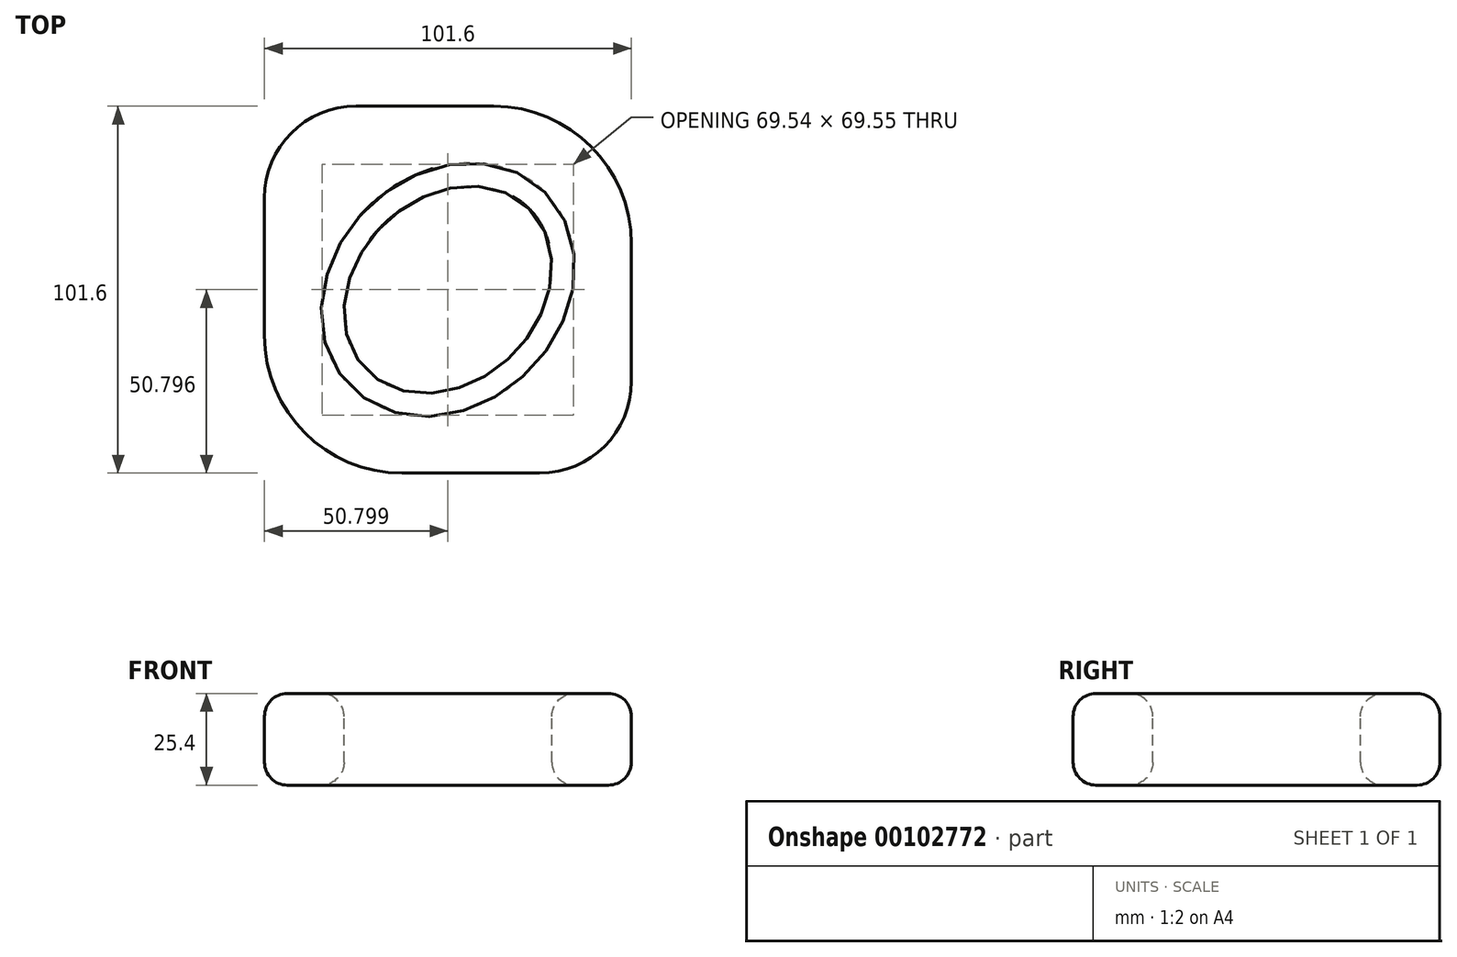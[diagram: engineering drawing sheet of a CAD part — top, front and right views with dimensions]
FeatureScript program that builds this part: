
annotation { "Feature Type Name" : "Feature", "Feature Type Description" : "" }
export const myFeature = defineFeature(function(context is Context, id is Id, definition is map)
    precondition{}
    {
        {
            var Q0;
            Q0=qCreatedBy(makeId("Top.planeOp"),FACE);
            var sketch = newSketch(context, id + "F0", { "sketchPlane" : qUnion([Q0])});
            skEllipse(sketch, "E0", {"center": v(0, 0) * mm, "majorRadius": 31.75 * mm, "minorRadius": 25.4 * mm, "majorAxis": v(0.7, 0.7)});
            skLineSegment(sketch, "E1", {"start": v(-22.45, -22.45) * mm, "end": v(22.45, 22.45) * mm, "construction": true});
            skLineSegment(sketch, "E2.bottom", {"start": v(50.8, -50.8) * mm, "end": v(-50.8, -50.8) * mm});
            skLineSegment(sketch, "E2.top", {"start": v(50.8, 50.8) * mm, "end": v(-50.8, 50.8) * mm});
            skLineSegment(sketch, "E2.left", {"start": v(50.8, -50.8) * mm, "end": v(50.8, 50.8) * mm});
            skLineSegment(sketch, "E2.right", {"start": v(-50.8, -50.8) * mm, "end": v(-50.8, 50.8) * mm});
            skSolve(sketch);
        }
        {
            var Q0;
            Q0=makeQuery(id+"F0.imprint","IMPRINT",FACE,{"disambiguationData":[TD([[makeQuery(id+"F0.imprint","IMPRINT",EDGE,{"derivedFrom":sQuery(id+"F0.wireOp",EDGE,"E0")}),-1.0]])]});
            extrude(context, id + "F1", {"entities" : qUnion([Q0]), "depth" : 25.4 * mm});
        }
        {
            var Q0;
            Q0=makeQuery(id+"F1.opExtrude","SWEPT_EDGE",EDGE,{"disambiguationData":[OSD([sQuery(id+"F0.wireOp",EDGE,"E2.bottom"),sQuery(id+"F0.wireOp",EDGE,"E2.left")])]});
            var Q1;
            Q1=makeQuery(id+"F1.opExtrude","SWEPT_EDGE",EDGE,{"disambiguationData":[OSD([sQuery(id+"F0.wireOp",EDGE,"E2.top"),sQuery(id+"F0.wireOp",EDGE,"E2.right")])]});
            fillet(context, id + "F2", {"entities" : qUnion([Q0, Q1]), "radius" : 25.4 * mm, "tangentPropagation" : true, "allowEdgeOverflow" : false});
        }
        {
            var Q0;
            Q0=makeQuery(id+"F1.opExtrude","SWEPT_EDGE",EDGE,{"disambiguationData":[OSD([sQuery(id+"F0.wireOp",EDGE,"E2.top"),sQuery(id+"F0.wireOp",EDGE,"E2.left")])]});
            var Q1;
            Q1=makeQuery(id+"F1.opExtrude","SWEPT_EDGE",EDGE,{"disambiguationData":[OSD([sQuery(id+"F0.wireOp",EDGE,"E2.bottom"),sQuery(id+"F0.wireOp",EDGE,"E2.right")])]});
            fillet(context, id + "F3", {"entities" : qUnion([Q0, Q1]), "radius" : 38.1 * mm, "tangentPropagation" : true, "allowEdgeOverflow" : false});
        }
        {
            var Q0;
            Q0=makeQuery(id+"F1.opExtrude","CAP_EDGE",EDGE,{"disambiguationData":[OSD([sQuery(id+"F0.wireOp",EDGE,"E2.bottom")])],"isStart":false});
            var Q1;
            Q1=makeQuery(id+"F1.opExtrude","CAP_EDGE",EDGE,{"disambiguationData":[OSD([sQuery(id+"F0.wireOp",EDGE,"E2.bottom")])],"isStart":true});
            var Q2;
            Q2=makeQuery(id+"F1.opExtrude","CAP_EDGE",EDGE,{"disambiguationData":[OSD([sQuery(id+"F0.wireOp",EDGE,"E0")])],"isStart":false});
            var Q3;
            Q3=makeQuery(id+"F1.opExtrude","CAP_EDGE",EDGE,{"disambiguationData":[OSD([sQuery(id+"F0.wireOp",EDGE,"E0")])],"isStart":true});
            fillet(context, id + "F4", {"entities" : qUnion([Q0, Q1, Q2, Q3]), "radius" : 6.35 * mm, "tangentPropagation" : true, "allowEdgeOverflow" : false});
        }
    });
